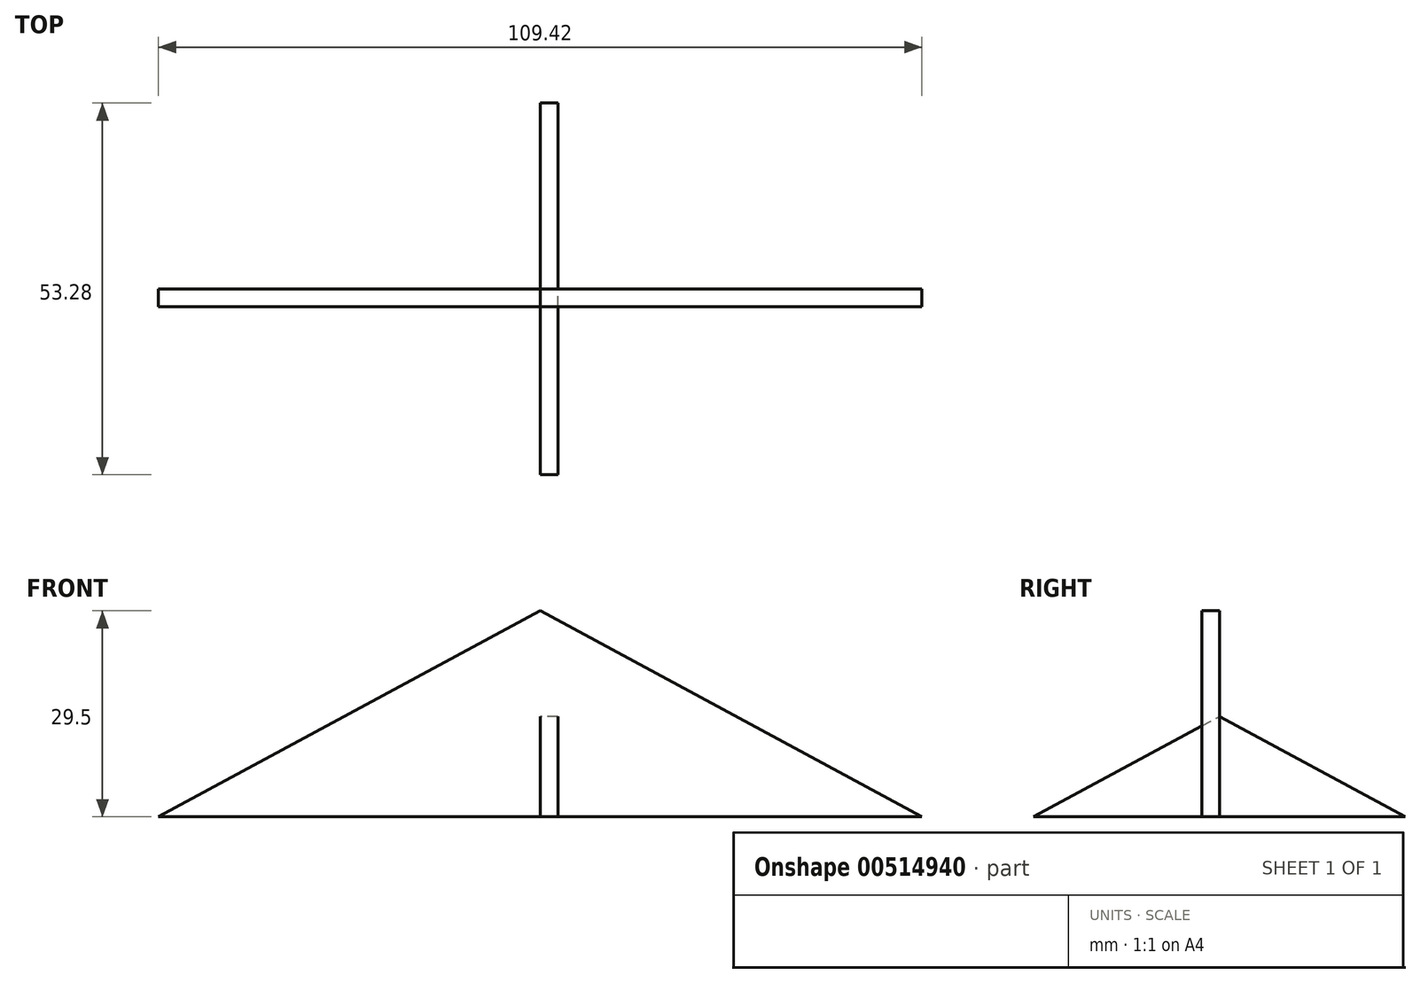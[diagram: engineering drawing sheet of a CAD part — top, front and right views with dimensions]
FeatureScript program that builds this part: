
annotation { "Feature Type Name" : "Feature", "Feature Type Description" : "" }
export const myFeature = defineFeature(function(context is Context, id is Id, definition is map)
    precondition{}
    {
        {
            var Q0;
            Q0=qCreatedBy(makeId("Front.planeOp"),FACE);
            var sketch = newSketch(context, id + "F0", { "sketchPlane" : qUnion([Q0])});
            skLineSegment(sketch, "E0", {"start": v(0, 0) * mm, "end": v(-54.71, 0) * mm});
            skLineSegment(sketch, "E1", {"start": v(-54.71, 0) * mm, "end": v(0, 29.5) * mm});
            skLineSegment(sketch, "E2", {"start": v(0, 29.5) * mm, "end": v(0, 0) * mm});
            skLineSegment(sketch, "E3.MirrorCS", {"start": v(54.71, 0) * mm, "end": v(0, 29.5) * mm});
            skLineSegment(sketch, "E4.MirrorCS", {"start": v(0, 0) * mm, "end": v(54.71, 0) * mm});
            skSolve(sketch);
        }
        {
            var Q0;
            Q0=qCreatedBy(makeId("Right.planeOp"),FACE);
            var sketch = newSketch(context, id + "F1", { "sketchPlane" : qUnion([Q0])});
            skLineSegment(sketch, "E5", {"start": v(0, 14.35) * mm, "end": v(0, 0) * mm});
            skLineSegment(sketch, "E6", {"start": v(0, 0) * mm, "end": v(26.64, 0) * mm});
            skLineSegment(sketch, "E7", {"start": v(26.64, 0) * mm, "end": v(0, 14.35) * mm});
            skLineSegment(sketch, "E8.MirrorCS", {"start": v(-26.64, 0) * mm, "end": v(0, 14.35) * mm});
            skLineSegment(sketch, "E9.MirrorCS", {"start": v(0, 0) * mm, "end": v(-26.64, 0) * mm});
            skSolve(sketch);
        }
        {
            var Q0;
            Q0=makeQuery(id+"F0.imprint","IMPRINT",FACE,{"disambiguationData":[TD([[makeQuery(id+"F0.imprint","IMPRINT",EDGE,{"derivedFrom":sQuery(id+"F0.wireOp",EDGE,"E2")}),1.0]])]});
            var Q1;
            Q1=makeQuery(id+"F0.imprint","IMPRINT",FACE,{"disambiguationData":[TD([[makeQuery(id+"F0.imprint","IMPRINT",EDGE,{"derivedFrom":sQuery(id+"F0.wireOp",EDGE,"E0")}),-1.0]])]});
            extrude(context, id + "F2", {"entities" : qUnion([Q0, Q1]), "depth" : 2.54 * mm, "offsetDistance" : 25.4 * mm});
        }
        {
            var Q0;
            Q0=makeQuery(id+"F1.imprint","IMPRINT",FACE,{"disambiguationData":[TD([[makeQuery(id+"F1.imprint","IMPRINT",EDGE,{"derivedFrom":sQuery(id+"F1.wireOp",EDGE,"E5")}),1.0]])]});
            var Q1;
            Q1=makeQuery(id+"F1.imprint","IMPRINT",FACE,{"disambiguationData":[TD([[makeQuery(id+"F1.imprint","IMPRINT",EDGE,{"derivedFrom":sQuery(id+"F1.wireOp",EDGE,"E5")}),-1.0]])]});
            extrude(context, id + "F3", {"entities" : qUnion([Q0, Q1]), "depth" : 2.54 * mm, "offsetDistance" : 25.4 * mm});
        }
    });
